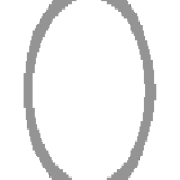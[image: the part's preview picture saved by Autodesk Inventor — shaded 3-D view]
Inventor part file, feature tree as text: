
AUTODESK INVENTOR PART (.ipt)
format: ipt  version: 2021 (Build 250183000, 183)  size: 109,568 bytes
history: native  units: in
note: dims shown in document units (in); Inventor stores cm internally (conversion verified against a paired STEP export)
features: other x4, sketch x3, plane x1
ambient origin geometry x8: Origin, YZ Plane, XZ Plane, XY Plane, X Axis, Y Axis, Z Axis, Center Point
bodies: Solid1 (feature_tree), Body (feature_tree)
feature tree (8):
  other  "Driven Length"
  other  "Frame Generator"
  other  "Start Plane"
  other  "End Plane"
  sketch  "Sketch"  dims[d2=32.7942in d4=-0.0in d5=32.7942in d6=0.12in d7=0.0in d10=90.0deg d9=32.7942in]
  sketch  "Sketch4"  dims[d0=1.0in]
  plane  "Work Plane4"
  sketch  "Sketch5"  dims[d1=0.065in]
